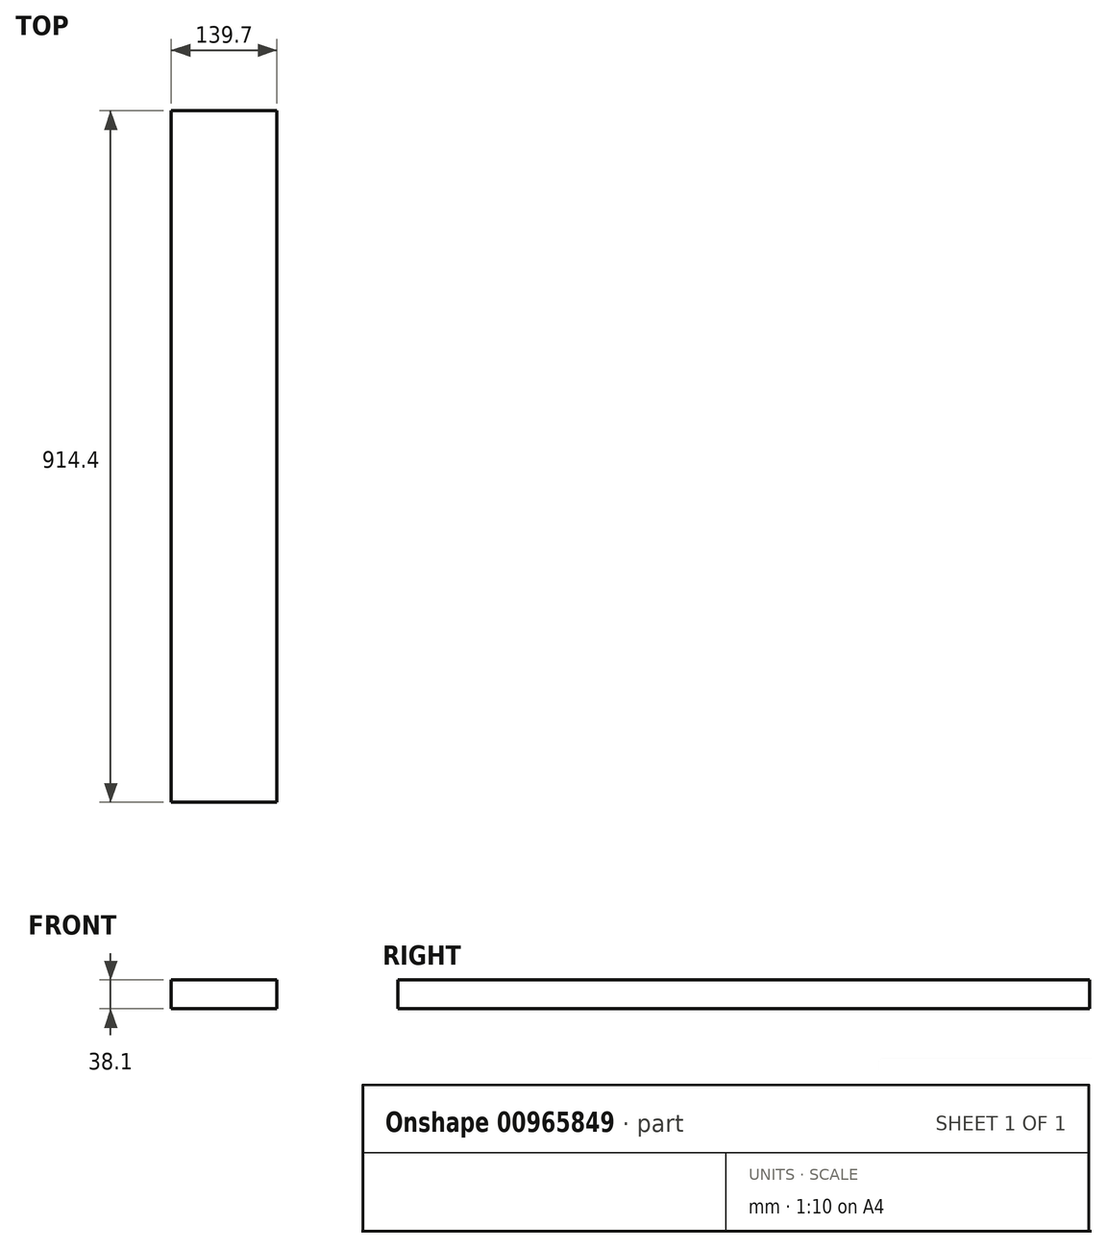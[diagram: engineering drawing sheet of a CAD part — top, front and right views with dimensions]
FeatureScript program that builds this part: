
annotation { "Feature Type Name" : "Feature", "Feature Type Description" : "" }
export const myFeature = defineFeature(function(context is Context, id is Id, definition is map)
    precondition{}
    {
        {
            var Q0;
            Q0=qCreatedBy(makeId("Front.planeOp"),FACE);
            var sketch = newSketch(context, id + "F0", { "sketchPlane" : qUnion([Q0])});
            skLineSegment(sketch, "E0.bottom", {"start": v(-63.78, -28.17) * mm, "end": v(75.92, -28.17) * mm});
            skLineSegment(sketch, "E0.top", {"start": v(-63.78, -66.27) * mm, "end": v(75.92, -66.27) * mm});
            skLineSegment(sketch, "E0.left", {"start": v(-63.78, -28.17) * mm, "end": v(-63.78, -66.27) * mm});
            skLineSegment(sketch, "E0.right", {"start": v(75.92, -28.17) * mm, "end": v(75.92, -66.27) * mm});
            skSolve(sketch);
        }
        {
            var Q0;
            Q0=makeQuery(id+"F0.imprint","IMPRINT",FACE,{"disambiguationData":[TD([[makeQuery(id+"F0.imprint","IMPRINT",EDGE,{"derivedFrom":sQuery(id+"F0.wireOp",EDGE,"E0.bottom")}),-1.0]])]});
            extrude(context, id + "F1", {"entities" : qUnion([Q0]), "depth" : 914.4 * mm, "offsetDistance" : 25.4 * mm});
        }
    });
